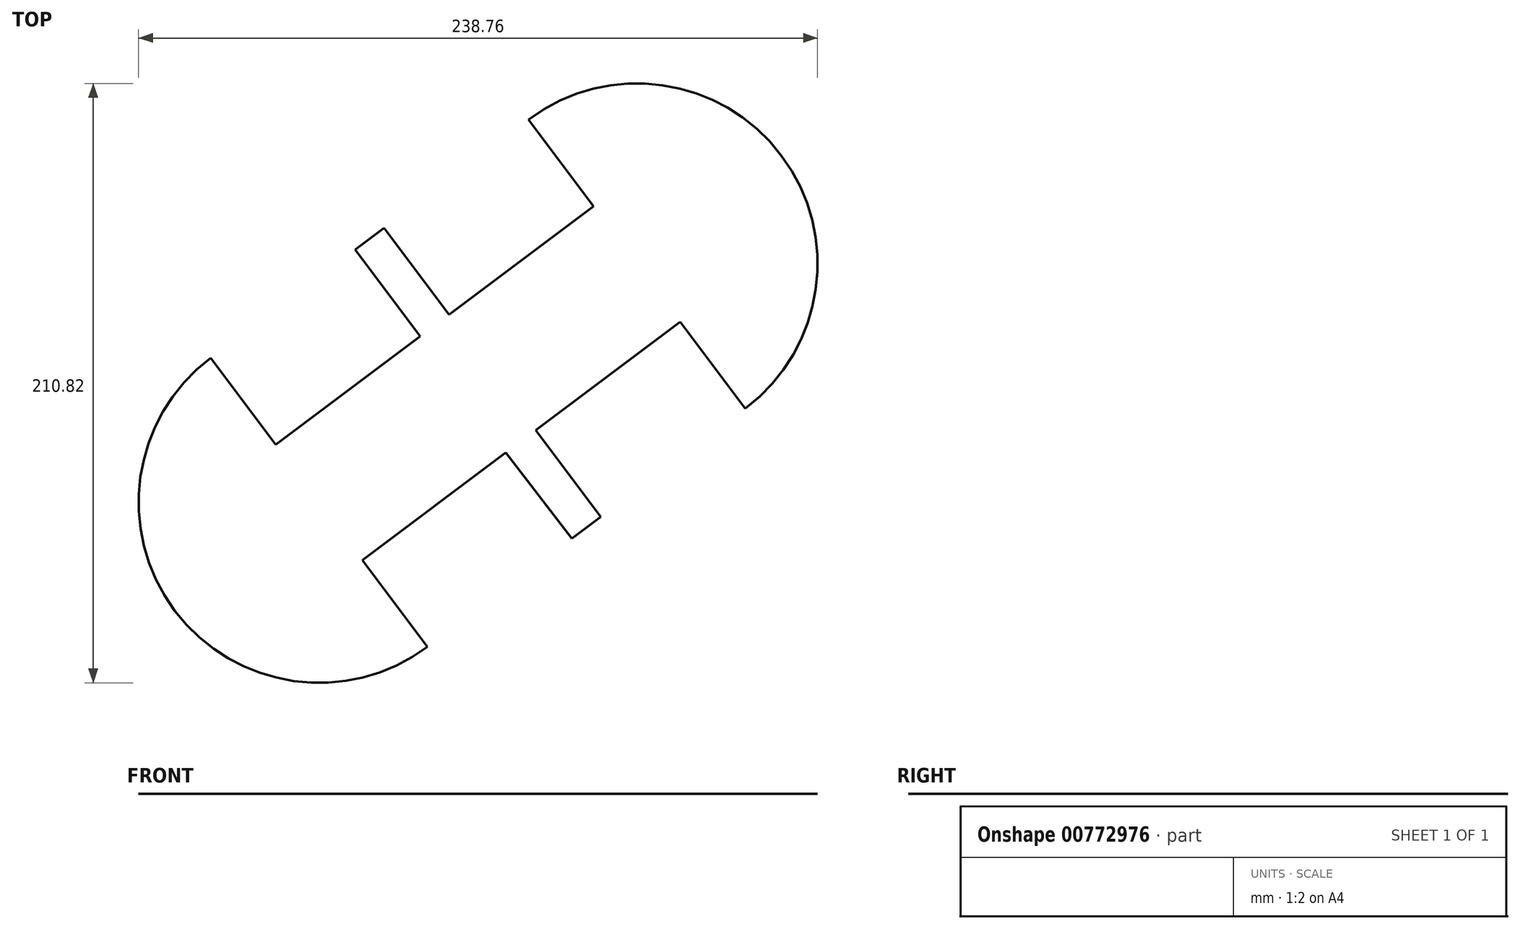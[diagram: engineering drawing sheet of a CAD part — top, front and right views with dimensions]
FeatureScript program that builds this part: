
annotation { "Feature Type Name" : "Feature", "Feature Type Description" : "" }
export const myFeature = defineFeature(function(context is Context, id is Id, definition is map)
    precondition{}
    {
        {
            var Q0;
            Q0=qCreatedBy(makeId("Top.planeOp"),FACE);
            var sketch = newSketch(context, id + "F0", { "sketchPlane" : qUnion([Q0])});
            skArc(sketch, "E0", {"start": v(76.2, -52.36) * mm, "mid": v(88.9, 36.54) * mm, "end": v(0, 49.24) * mm});
            skPoint(sketch, "E1.orphan", {"position": v(101.58, 0) * mm});
            skLineSegment(sketch, "E2", {"start": v(0, 49.24) * mm, "end": v(22.86, 18.76) * mm});
            skLineSegment(sketch, "E3.MirrorCS", {"start": v(-111.76, -34.58) * mm, "end": v(-88.9, -65.06) * mm});
            skArc(sketch, "E4.MirrorCS", {"start": v(-35.56, -136.18) * mm, "mid": v(-124.46, -123.48) * mm, "end": v(-111.76, -34.58) * mm});
            skLineSegment(sketch, "E5", {"start": v(-88.9, -65.06) * mm, "end": v(-38.1, -26.96) * mm});
            skLineSegment(sketch, "E6", {"start": v(-58.42, -105.7) * mm, "end": v(-22.97, -79.12) * mm});
            skLineSegment(sketch, "E7", {"start": v(-38.1, -26.96) * mm, "end": v(-60.96, 3.52) * mm});
            skLineSegment(sketch, "E8", {"start": v(-60.96, 3.52) * mm, "end": v(-50.8, 11.14) * mm});
            skLineSegment(sketch, "E9", {"start": v(-50.8, 11.14) * mm, "end": v(-27.94, -19.34) * mm});
            skLineSegment(sketch, "E10.MirrorCS", {"start": v(15.24, -98.08) * mm, "end": v(25.4, -90.46) * mm});
            skLineSegment(sketch, "E11.trimOffspring", {"start": v(-58.42, -105.7) * mm, "end": v(-35.56, -136.18) * mm});
            skLineSegment(sketch, "E12.trimOffspring", {"start": v(53.34, -21.88) * mm, "end": v(76.2, -52.36) * mm});
            skLineSegment(sketch, "E13.trimOffspring", {"start": v(-27.94, -19.34) * mm, "end": v(22.86, 18.76) * mm});
            skLineSegment(sketch, "E14.trimOffspring", {"start": v(2.54, -59.98) * mm, "end": v(53.34, -21.88) * mm});
            skLineSegment(sketch, "E15", {"start": v(-22.97, -79.12) * mm, "end": v(-8.11, -67.97) * mm});
            skLineSegment(sketch, "E16", {"start": v(25.4, -90.46) * mm, "end": v(2.54, -59.98) * mm});
            skLineSegment(sketch, "E17", {"start": v(15.24, -98.08) * mm, "end": v(-8.11, -67.97) * mm});
            skSolve(sketch);
        }
        {
            var Q0;
            Q0=makeQuery(id+"F0.imprint","IMPRINT",FACE,{"disambiguationData":[TD([[makeQuery(id+"F0.imprint","IMPRINT",EDGE,{"derivedFrom":sQuery(id+"F0.wireOp",EDGE,"E0")}),1.0]])]});
            extrude(context, id + "F1", {"entities" : qUnion([Q0]), "depth" : 1 / 203.2 * mm, "offsetDistance" : 25.4 * mm});
        }
        {
            var Q0;
            Q0=makeQuery(id+"F1.opExtrude","SWEPT_FACE",FACE,{"disambiguationData":[OSD([sQuery(id+"F0.wireOp",EDGE,"E6"),sQuery(id+"F0.wireOp",EDGE,"E15")])]});
            var sketch = newSketch(context, id + "F2", { "sketchPlane" : qUnion([Q0])});
            skCircle(sketch, "E18", {"center": v(-78.71, -15.87) * mm, "radius": 6.35 * mm});
            skLineSegment(sketch, "E19", {"start": v(-78.71, -15.87) * mm, "end": v(-78.71, 3.18) * mm});
            skSolve(sketch);
        }
        {
            var Q0;
            Q0 = qSketchRegion(id + "F2", true);
            var Q1;
            Q1=sQuery(id+"F2.wireOp",EDGE,"E18");
            extrude(context, id + "F3", {"entities" : qUnion([Q0]), "operationType" : NewBodyOperationType.REMOVE, "surfaceEntities" : qUnion([Q1]), "oppositeDirection" : true, "depth" : 50.8 * mm, "offsetDistance" : 25.4 * mm});
        }
        {
            var Q0;
            Q0=makeQuery(id+"F1.opExtrude","SWEPT_FACE",FACE,{"disambiguationData":[OSD([sQuery(id+"F0.wireOp",EDGE,"E13.trimOffspring")])]});
            var sketch = newSketch(context, id + "F4", { "sketchPlane" : qUnion([Q0])});
            skCircle(sketch, "E20", {"center": v(2.2, -15.87) * mm, "radius": 6.35 * mm});
            skPoint(sketch, "E20.centerSnap0", {"position": v(2.2, 3.17) * mm});
            skSolve(sketch);
        }
        {
            var Q0;
            Q0=makeQuery(id+"F4.imprint","IMPRINT",FACE,{"disambiguationData":[TD([[makeQuery(id+"F4.imprint","IMPRINT",EDGE,{"derivedFrom":sQuery(id+"F4.wireOp",EDGE,"E20")}),1.0]])]});
            var Q1;
            Q1=sQuery(id+"F4.wireOp",EDGE,"E20");
            extrude(context, id + "F5", {"entities" : qUnion([Q0]), "operationType" : NewBodyOperationType.REMOVE, "surfaceEntities" : qUnion([Q1]), "oppositeDirection" : true, "depth" : 50.8 * mm, "offsetDistance" : 25.4 * mm});
        }
    });
